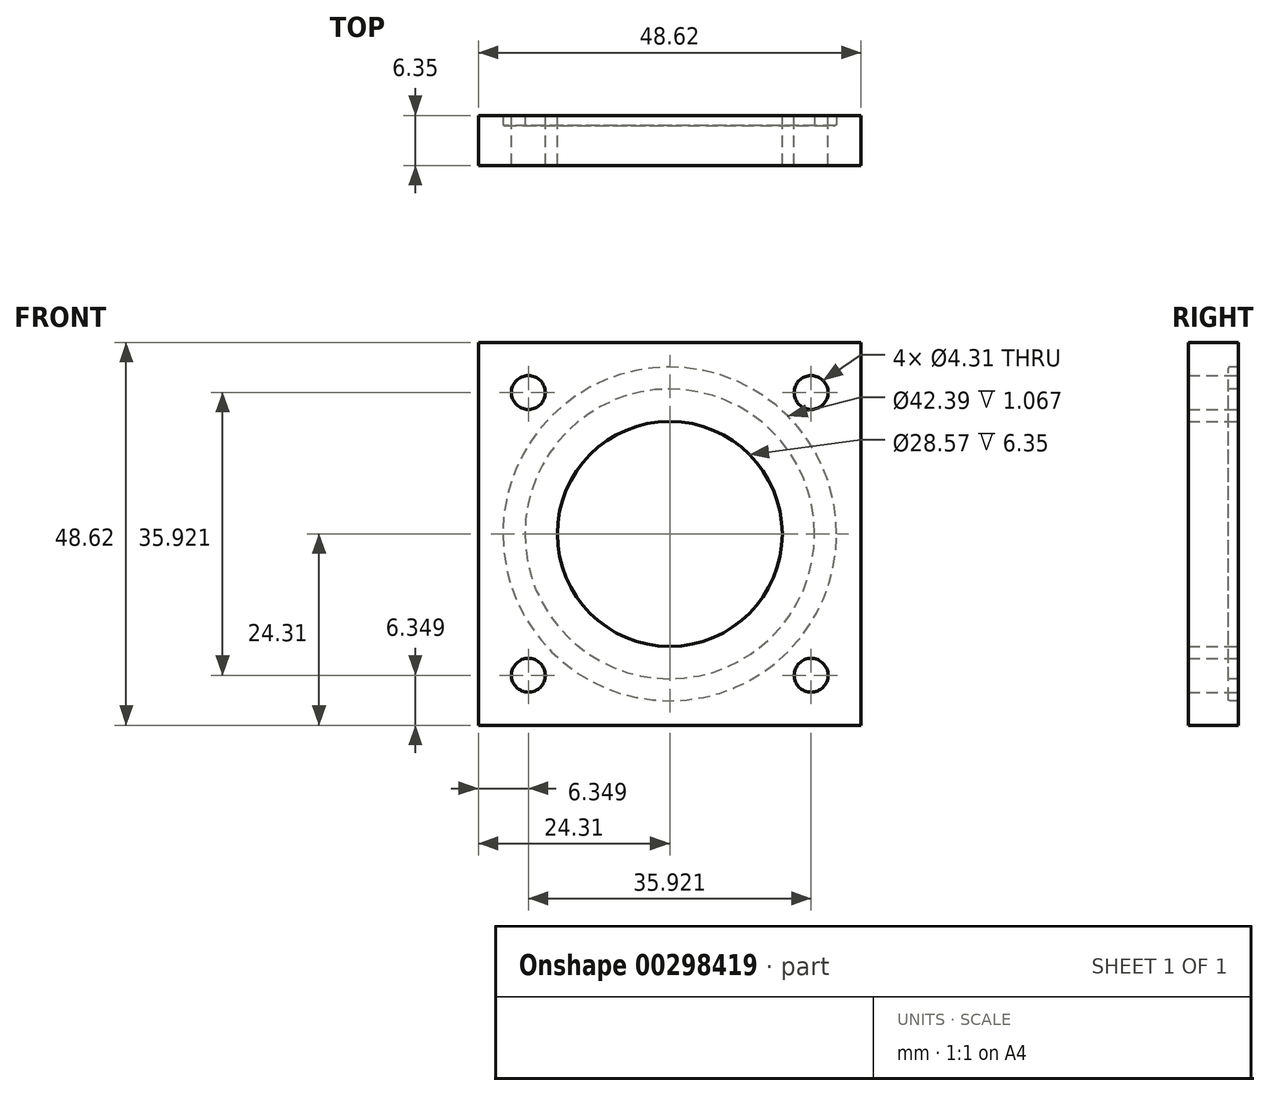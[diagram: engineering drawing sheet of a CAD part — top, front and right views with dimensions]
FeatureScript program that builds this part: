
annotation { "Feature Type Name" : "Feature", "Feature Type Description" : "" }
export const myFeature = defineFeature(function(context is Context, id is Id, definition is map)
    precondition{}
    {
        {
            var Q0;
            Q0=qCreatedBy(makeId("Front.planeOp"),FACE);
            var sketch = newSketch(context, id + "F0", { "sketchPlane" : qUnion([Q0])});
            skLineSegment(sketch, "E0.bottom", {"start": v(24.31, 24.31) * mm, "end": v(-24.31, 24.31) * mm});
            skLineSegment(sketch, "E0.top", {"start": v(24.31, -24.31) * mm, "end": v(-24.31, -24.31) * mm});
            skLineSegment(sketch, "E0.left", {"start": v(24.31, 24.31) * mm, "end": v(24.31, -24.31) * mm});
            skLineSegment(sketch, "E0.right", {"start": v(-24.31, 24.31) * mm, "end": v(-24.31, -24.31) * mm});
            skPoint(sketch, "E0.middle", {"position": v(0, 0) * mm});
            skCircle(sketch, "E1", {"center": v(-17.96, -17.96) * mm, "radius": 2.15 * mm});
            skCircle(sketch, "E2", {"center": v(0, 0) * mm, "radius": 25.4 * mm, "construction": true});
            skLineSegment(sketch, "E3", {"start": v(-17.96, -17.96) * mm, "end": v(0, 0) * mm, "construction": true});
            skCircle(sketch, "E4.1.0", {"center": v(17.96, -17.96) * mm, "radius": 2.15 * mm});
            skCircle(sketch, "E4.2.0", {"center": v(17.96, 17.96) * mm, "radius": 2.15 * mm});
            skCircle(sketch, "E4.3.0", {"center": v(-17.96, 17.96) * mm, "radius": 2.15 * mm});
            skSolve(sketch);
        }
        {
            var Q0;
            Q0=makeQuery(id+"F0.imprint","IMPRINT",FACE,{"disambiguationData":[TD([[makeQuery(id+"F0.imprint","IMPRINT",EDGE,{"derivedFrom":makeQuery(id+"FBOyUSbzv9L5WvW_0.merge.FRwLIMHdycvGu99_1.1.FLy9HZHc7Aeuiqs_1.boolean.opBoolean","COPY",EDGE,{"derivedFrom":makeQuery(id+"FBOyUSbzv9L5WvW_0.merge.FRwLIMHdycvGu99_1.1.FLy9HZHc7Aeuiqs_1.opExtrude","CAP_EDGE",EDGE,{"disambiguationData":[OSD([sQuery(id+"FBOyUSbzv9L5WvW_0.merge.Fd7ioR1l4POb1cx_1.wireOp",EDGE,"KR8DdwEu-s3LD-aGZ0-tnwe-elepxOLVecz2")])],"isStart":true})})}),-1.0]])]});
            var Q1;
            Q1=makeQuery(id+"F0.imprint","IMPRINT",FACE,{"disambiguationData":[TD([[makeQuery(id+"F0.imprint","IMPRINT",EDGE,{"derivedFrom":sQuery(id+"F0.wireOp",EDGE,"E0.bottom")}),1.0]])]});
            extrude(context, id + "F1", {"entities" : qUnion([Q0, Q1]), "depth" : 6.35 * mm});
        }
        {
            var Q0;
            Q0=makeQuery(id+"F1.opExtrude","CAP_EDGE",EDGE,{"disambiguationData":[OSD([sQuery(id+"F0.wireOp",EDGE,"E0.right")])],"isStart":false});
            cPoint(context, id + "F2", {"entities" : qUnion([Q0]), "parameter" : 0.5});
        }
        {
            var Q0;
            Q0=makeQuery(id+"F1.opExtrude","CAP_EDGE",EDGE,{"disambiguationData":[OSD([sQuery(id+"F0.wireOp",EDGE,"E0.left")])],"isStart":false});
            cPoint(context, id + "F3", {"entities" : qUnion([Q0]), "parameter" : 0.5});
        }
        {
            var Q0;
            Q0=makeQuery(id+"F1.opExtrude","CAP_EDGE",EDGE,{"disambiguationData":[OSD([sQuery(id+"F0.wireOp",EDGE,"E0.left")])],"isStart":true});
            cPoint(context, id + "F4", {"entities" : qUnion([Q0]), "parameter" : 0.5});
        }
        {
            var Q0;
            Q0=qCreatedBy(id+"F2",VERTEX);
            var Q1;
            Q1=qCreatedBy(id+"F3",VERTEX);
            var Q2;
            Q2=qCreatedBy(id+"F4",VERTEX);
            cPlane(context, id + "F5", {"entities" : qUnion([Q0, Q1, Q2]), "cplaneType" : CPlaneType.THREE_POINT, "offset" : 25.4 * mm, "width" : 152.4 * mm, "height" : 152.4 * mm});
        }
        {
            var Q0;
            Q0=qCreatedBy(id+"F5.planeOp",FACE);
            var sketch = newSketch(context, id + "F6", { "sketchPlane" : qUnion([Q0])});
            skLineSegment(sketch, "E5.bottom", {"start": v(-18.4, 0) * mm, "end": v(-21.2, 0) * mm});
            skLineSegment(sketch, "E5.top", {"start": v(-18.4, 1.27) * mm, "end": v(-21.2, 1.27) * mm});
            skLineSegment(sketch, "E5.left", {"start": v(-18.4, 0) * mm, "end": v(-18.4, 1.27) * mm});
            skLineSegment(sketch, "E5.right", {"start": v(-21.2, 0) * mm, "end": v(-21.2, 1.27) * mm});
            skPoint(sketch, "E5.middle", {"position": v(-19.8, 0.64) * mm});
            skLineSegment(sketch, "E6", {"start": v(0, -20.02) * mm, "end": v(0, 19.12) * mm, "construction": true});
            skSolve(sketch);
        }
        {
            var Q0;
            Q0=qSketchRegion(id+"F6",true);
            var Q1;
            Q1=sQuery(id+"F6.wireOp",EDGE,"E6");
            revolve(context, id + "F7", {"operationType" : NewBodyOperationType.REMOVE, "entities" : qUnion([Q0]), "axis" : qUnion([Q1]), "revolveType" : RevolveType.FULL, "oppositeDirection" : true});
        }
        {
            var Q0;
            Q0=makeQuery(id+"F7.boolean.opBoolean","COPY",EDGE,{"derivedFrom":makeQuery(id+"F7.opRevolve","SWEPT_EDGE",EDGE,{"disambiguationData":[OSD([sQuery(id+"F6.wireOp",EDGE,"E5.top"),sQuery(id+"F6.wireOp",EDGE,"E5.right")])]})});
            var Q1;
            Q1=makeQuery(id+"F7.boolean.opBoolean","COPY",EDGE,{"derivedFrom":makeQuery(id+"F7.opRevolve","SWEPT_EDGE",EDGE,{"disambiguationData":[OSD([sQuery(id+"F6.wireOp",EDGE,"E5.bottom"),sQuery(id+"F6.wireOp",EDGE,"E5.left")])]})});
            fillet(context, id + "F8", {"entities" : qUnion([Q0, Q1]), "radius" : 0.2 * mm, "tangentPropagation" : true, "allowEdgeOverflow" : false});
        }
        {
            var Q0;
            Q0=makeQuery(id+"F7.boolean.opBoolean","SPLIT",FACE,{"disambiguationData":[TD([makeQuery(id+"F7.opRevolve","SWEPT_FACE",FACE,{"disambiguationData":[OSD([sQuery(id+"F6.wireOp",EDGE,"E5.left")])]})])],"derivedFrom":makeQuery(id+"F1.opExtrude","CAP_FACE",FACE,{"disambiguationData":[OSD([sQuery(id+"F0.wireOp",EDGE,"E0.bottom"),sQuery(id+"F0.wireOp",EDGE,"E0.top"),sQuery(id+"F0.wireOp",EDGE,"E0.left"),sQuery(id+"F0.wireOp",EDGE,"E0.right"),sQuery(id+"F0.wireOp",EDGE,"E1"),sQuery(id+"F0.wireOp",EDGE,"E4.1.0"),sQuery(id+"F0.wireOp",EDGE,"E4.2.0"),sQuery(id+"F0.wireOp",EDGE,"E4.3.0")])],"isStart":true})});
            var sketch = newSketch(context, id + "F9", { "sketchPlane" : qUnion([Q0])});
            skCircle(sketch, "E7", {"center": v(0, 0) * mm, "radius": 14.29 * mm});
            skSolve(sketch);
        }
        {
            var Q0;
            Q0=makeQuery(id+"F9.imprint","IMPRINT",FACE,{"disambiguationData":[TD([[makeQuery(id+"F9.imprint","IMPRINT",EDGE,{"derivedFrom":sQuery(id+"F9.wireOp",EDGE,"E7")}),1.0]])]});
            extrude(context, id + "F10", {"entities" : qUnion([Q0]), "operationType" : NewBodyOperationType.REMOVE, "endBound" : BoundingType.THROUGH_ALL, "oppositeDirection" : true, "depth" : 25.4 * mm});
        }
    });
